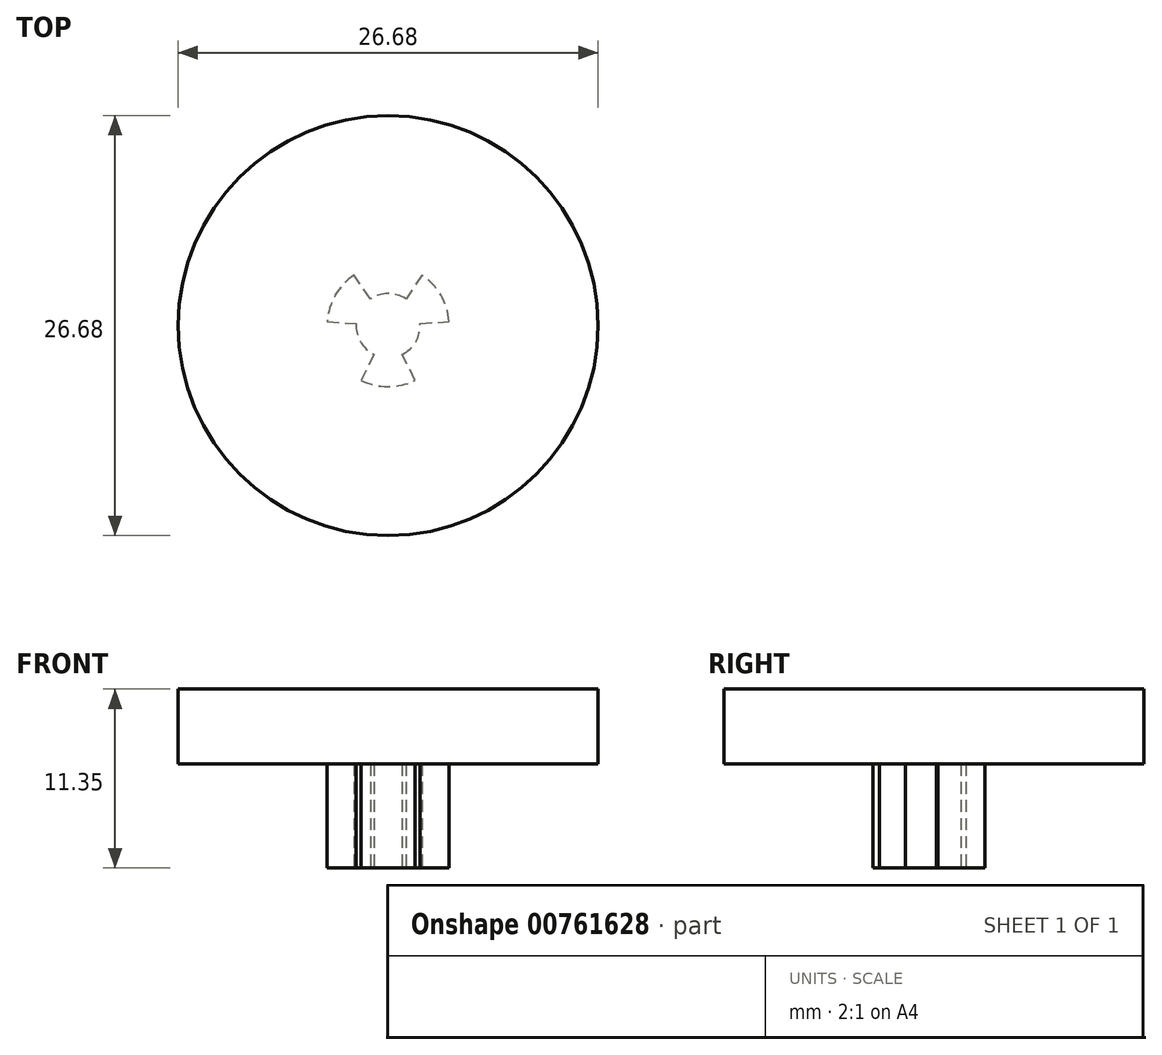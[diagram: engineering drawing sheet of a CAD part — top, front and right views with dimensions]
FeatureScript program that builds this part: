
annotation { "Feature Type Name" : "Feature", "Feature Type Description" : "" }
export const myFeature = defineFeature(function(context is Context, id is Id, definition is map)
    precondition{}
    {
        {
            var Q0;
            Q0=qCreatedBy(makeId("Top.planeOp"),FACE);
            var sketch = newSketch(context, id + "F0", { "sketchPlane" : qUnion([Q0])});
            skCircle(sketch, "E0", {"center": v(0, 0) * mm, "radius": 13.34 * mm});
            skCircle(sketch, "E1", {"center": v(0, 0) * mm, "radius": 3.87 * mm});
            skCircle(sketch, "E2", {"center": v(0, 0) * mm, "radius": 2.03 * mm});
            skLineSegment(sketch, "E3", {"start": v(2.03, 0) * mm, "end": v(3.87, 0) * mm});
            skLineSegment(sketch, "E4", {"start": v(2.03, -0.13) * mm, "end": v(3.87, -0.25) * mm});
            skLineSegment(sketch, "E5", {"start": v(3.87, -0.25) * mm, "end": v(2.03, -0.13) * mm});
            skLineSegment(sketch, "E6", {"start": v(2.03, 0.13) * mm, "end": v(3.87, 0.25) * mm});
            skLineSegment(sketch, "E7.1.0", {"start": v(0.9, 1.82) * mm, "end": v(1.71, 3.47) * mm});
            skLineSegment(sketch, "E7.1.1", {"start": v(2.15, 3.22) * mm, "end": v(1.13, 1.69) * mm});
            skLineSegment(sketch, "E7.2.0", {"start": v(-1.13, 1.69) * mm, "end": v(-2.15, 3.22) * mm});
            skLineSegment(sketch, "E7.2.1", {"start": v(-1.71, 3.47) * mm, "end": v(-0.9, 1.82) * mm});
            skLineSegment(sketch, "E7.3.0", {"start": v(-2.03, -0.13) * mm, "end": v(-3.87, -0.25) * mm});
            skLineSegment(sketch, "E7.3.1", {"start": v(-3.87, 0.25) * mm, "end": v(-2.03, 0.13) * mm});
            skLineSegment(sketch, "E7.4.0", {"start": v(-0.9, -1.82) * mm, "end": v(-1.71, -3.47) * mm});
            skLineSegment(sketch, "E7.4.1", {"start": v(-2.15, -3.22) * mm, "end": v(-1.13, -1.69) * mm});
            skLineSegment(sketch, "E7.5.0", {"start": v(1.13, -1.69) * mm, "end": v(2.15, -3.22) * mm});
            skLineSegment(sketch, "E7.5.1", {"start": v(1.71, -3.47) * mm, "end": v(0.9, -1.82) * mm});
            skSolve(sketch);
        }
        {
            var Q0;
            {var subQ0=sQuery(id+"F0.wireOp",EDGE,"E7.4.0");Q0=makeQuery(id+"F0.imprint","IMPRINT",FACE,{"disambiguationData":[TD([[makeQuery(id+"F0.imprint","IMPRINT",EDGE,{"derivedFrom":subQ0}),1.0]])]});}
            var Q1;
            {var subQ0=sQuery(id+"F0.wireOp",EDGE,"E7.2.0");Q1=makeQuery(id+"F0.imprint","IMPRINT",FACE,{"disambiguationData":[TD([[makeQuery(id+"F0.imprint","IMPRINT",EDGE,{"derivedFrom":subQ0}),1.0]])]});}
            var Q2;
            {var subQ0=sQuery(id+"F0.wireOp",EDGE,"E6");Q2=makeQuery(id+"F0.imprint","IMPRINT",FACE,{"disambiguationData":[TD([[makeQuery(id+"F0.imprint","IMPRINT",EDGE,{"derivedFrom":subQ0}),1.0]])]});}
            var Q3;
            {var subQ0=sQuery(id+"F0.wireOp",EDGE,"E2");var subQ8=makeQuery(id+"F0.imprint","INTERSECT",VERTEX,{"derivedFrom":[subQ0,sQuery(id+"F0.wireOp",EDGE,"E3")]});Q3=makeQuery(id+"F0.imprint","IMPRINT",FACE,{"disambiguationData":[TD([[makeQuery(id+"F0.imprint","IMPRINT",EDGE,{"disambiguationData":[TD([[subQ8,-1.0]])],"derivedFrom":subQ0}),1.0]])]});}
            extrude(context, id + "F1", {"entities" : qUnion([Q0, Q1, Q2, Q3]), "depth" : 6.6 * mm, "offsetDistance" : 25.4 * mm});
        }
        {
            var Q0;
            Q0=makeQuery(id+"F1.opExtrude","CAP_FACE",FACE,{"disambiguationData":[OSD([sQuery(id+"F0.wireOp",EDGE,"E1"),sQuery(id+"F0.wireOp",EDGE,"E2"),sQuery(id+"F0.wireOp",EDGE,"E6"),sQuery(id+"F0.wireOp",EDGE,"E7.1.1"),sQuery(id+"F0.wireOp",EDGE,"E7.2.0"),sQuery(id+"F0.wireOp",EDGE,"E7.3.1"),sQuery(id+"F0.wireOp",EDGE,"E7.4.0"),sQuery(id+"F0.wireOp",EDGE,"E7.5.1")])],"isStart":false});
            var sketch = newSketch(context, id + "F2", { "sketchPlane" : qUnion([Q0])});
            skCircle(sketch, "E8", {"center": v(0, 0) * mm, "radius": 13.33 * mm});
            skSolve(sketch);
        }
        {
            var Q0;
            Q0 = qSketchRegion(id + "F2", true);
            extrude(context, id + "F3", {"entities" : qUnion([Q0]), "operationType" : NewBodyOperationType.ADD, "depth" : 4.75 * mm, "offsetDistance" : 25.4 * mm});
        }
    });
